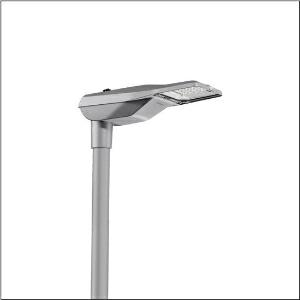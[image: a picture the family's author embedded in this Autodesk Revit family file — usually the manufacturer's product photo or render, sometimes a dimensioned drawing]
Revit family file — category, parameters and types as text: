
# Revit family: streetlight_sl_21_micro___st1_0a_5xe1d33s08db_38a0
name_source: partatom
category: Lighting Fixtures
units: mm (PartAtom-declared; Revit-internal decimal feet)

## family parameters
Cut with Voids When Loaded = No
Host = Face
Light Source = No
Part Type = Normal
Room Calculation Point = No
Round Connector Dimension = Use Diameter
Shared = No

## types (1)
- --- (1 x LED, 5110 lm, 39.1 W, 3000K)
    Apparent Load = 39 VA
    CIE Flux Codes = 37 72 97 100 100
    Color Rendering = 70
    Color Temperature = 3000K
    Default Elevation = 1800 mm
    Description = Streetlight SL 21 micro, mast luminaire, primary light control with lens, of PMMA, primary optical cover: cover, of toughened safety glass, transparent, light distribution: ST1.0a, light emission: direct distribution, primary light characteristic: asymmetric, installation type: side-entry, post-top, LED, High Power LED, rated luminous flux: 5.110lm, luminous efficacy: 131lm/W, light colour: 730, colour temperature: 3000K, control: flexible luminous flux parameterisation, time-dependent luminous flux control, constant luminous flux control, overheat protection, pre-setting: logarithmic dimming characteristic, mains connection: 220..240V, AC, 50/60Hz, start of lifetime: 39W, end of service life: 41W, reduction: 18W, luminaire housing, of diecast aluminium, powder-coated, Siteco® metallic grey (DB 702S), corrosivity category C5 mid according to DIN EN ISO 12944, please order mast flange separately, inclination adjustable: 0°, 5°, 10°, 15°, sealing non-destructively replaceable, multi-level sealing system, length: 528mm, width: 235mm, height: 110mm, mast flange for spigot size: 42mm (side-entry): 5XC10008XM4, 60/48mm (side-entry/post-top): 5XC10108XM2, 76/60mm (side-entry/post-top): 5XC10108XM1, Smart Interface above, protection rating (complete): IP66, insulation class (complete): insulation class II (safety insulation), certification: CE, ENEC, ENEC+, VDE, impact resistance: IK09, permissible operating ambient temperature for outdoor applications: -40..+50°C, standard-compliant lighting for roads and squares, packaging unit: 1 piece

Light Distribution: ST1.0a
    Height = 110 mm
    Lamp = 1 x LED
    Lamp Light Flux = 5110 lm
    Lamp Power = 39.1 W
    Lamp count = 1
    Length = 528 mm
    Luminous efficacy = 131 lm/W
    Manufacturer = Siteco
    ModVariant = No
    Model = 5XE1D33S08DB
    Number of Poles = 1
    OnlyDefault = Yes
    Power Factor = 1
    Product Name = Streetlight SL 21 micro | ST1.0a
    Product group = mast luminaire | pylon top
    ProductGroupID = 6100
    Protection Class = Protection class II
    Protection Degree = IP 66
    RLX_Detail_Level = 1
    RLX_Emergency_Light_Flux = 0 lm
    RLX_Emergency_Type = 0
    RLX_Emergency_Type_DB = No
    RlxData = <blob elided: 98765 chars, md5=de0bada5>
    Socket = socket
    Standby Power = 0 W
    System Light Flux = 5110 lm
    System Power = 39 W
    Type Comments = factory setting: luminous flux: 100 % | dim-lin: 254 | 765 mA
    Type Image = l_1277292.jpg
    URL = http://relux.com
    VarID = @adj_126207
    Voltage = 0 V
    Weight = 0.00 kg
    Width = 235 mm

## geometry (parser evidence)
native form markers: Blend x4, Sweep x8
no freeform markers — native parametric forms only
